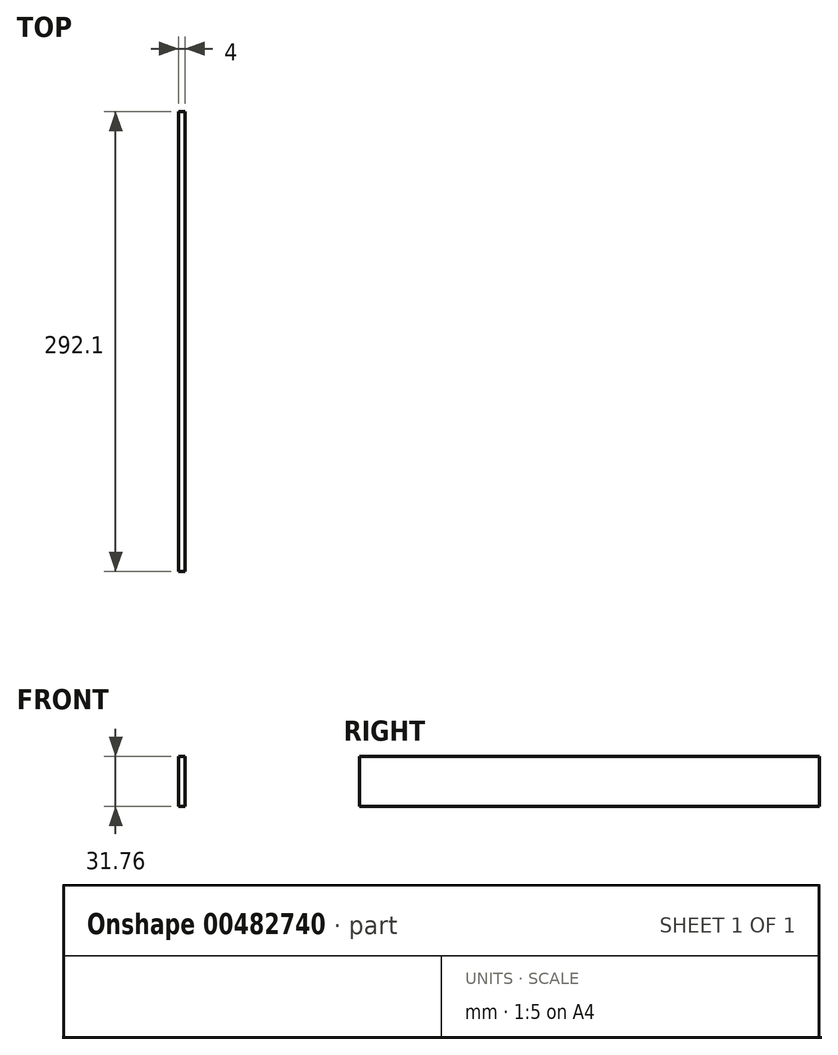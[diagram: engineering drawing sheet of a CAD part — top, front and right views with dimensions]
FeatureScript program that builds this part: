
annotation { "Feature Type Name" : "Feature", "Feature Type Description" : "" }
export const myFeature = defineFeature(function(context is Context, id is Id, definition is map)
    precondition{}
    {
        {
            var Q0;
            Q0=qCreatedBy(makeId("Right.planeOp"),FACE);
            var sketch = newSketch(context, id + "F0", { "sketchPlane" : qUnion([Q0])});
            skLineSegment(sketch, "E0.bottom", {"start": v(146.05, 15.88) * mm, "end": v(-146.05, 15.88) * mm});
            skLineSegment(sketch, "E0.top", {"start": v(146.05, -15.88) * mm, "end": v(-146.05, -15.88) * mm});
            skLineSegment(sketch, "E0.left", {"start": v(146.05, 15.88) * mm, "end": v(146.05, -15.88) * mm});
            skLineSegment(sketch, "E0.right", {"start": v(-146.05, 15.88) * mm, "end": v(-146.05, -15.88) * mm});
            skPoint(sketch, "E0.middle", {"position": v(0, 0) * mm});
            skSolve(sketch);
        }
        {
            var Q0;
            Q0=makeQuery(id+"F0.imprint","IMPRINT",FACE,{"disambiguationData":[TD([[makeQuery(id+"F0.imprint","IMPRINT",EDGE,{"derivedFrom":sQuery(id+"F0.wireOp",EDGE,"E0.bottom")}),1.0]])]});
            extrude(context, id + "F1", {"entities" : qUnion([Q0]), "depth" : 4 * mm});
        }
    });
